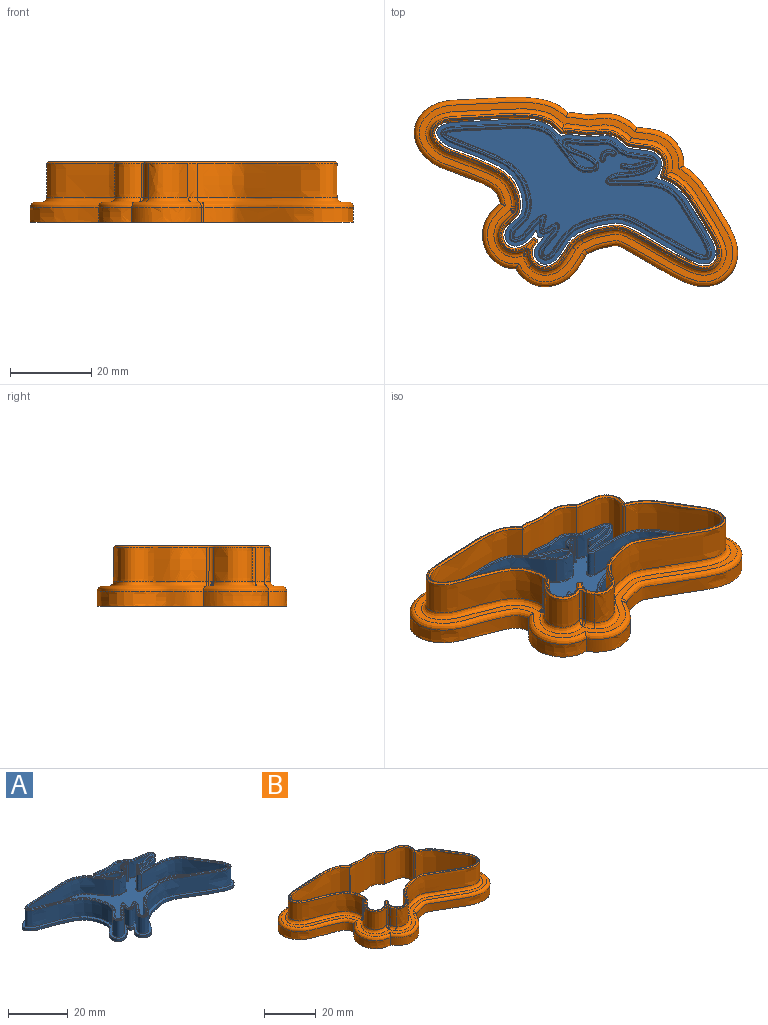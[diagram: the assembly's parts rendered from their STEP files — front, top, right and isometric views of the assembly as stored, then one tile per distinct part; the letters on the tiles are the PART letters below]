
ASSEMBLY  parts=2 mates=1
PART A: 95 faces, bbox 69x37.9x8.3 mm
  f0: plane 64.33x31.4mm, normal (0,0,1), area 715.8mm2, adj f40,f41,f42,f43,f45,f46,f47,f48
  f1: plane 68.72x35.77mm, normal (0,0,1), area 203.8mm2, adj f2,f3,f4,f5,f7,f8,f9,f10
  f2: extruded ~33.7x21.08mm, area 61mm2, adj f1,f3,f5,f6
  f3: extruded ~8.98x7.79mm, area 14.8mm2, adj f1,f2,f4,f6
  f4: extruded ~15.66x2.98mm, area 16.7mm2, adj f1,f3,f5,f6
  f5: extruded ~35.59x34.48mm, area 107.2mm2, adj f1,f2,f4,f6
  f6: plane 68.72x35.77mm, normal (0,0,-1), area 1212.7mm2, adj f2,f3,f4,f5
  f7: extruded ~14.82x6.75mm, area 110.2mm2, adj f1,f8,f26,f93
  f8: extruded ~6.75x0.94mm, area 8.2mm2, adj f1,f7,f9,f94
  f9: extruded ~29.13x29mm, area 500.5mm2, adj f1,f8,f10,f92
  f10: extruded ~12.57x9.63mm, area 227mm2, adj f1,f9,f11,f90
  f11: extruded ~33.3x19.43mm, area 477.3mm2, adj f1,f10,f12,f88
  f12: extruded ~6.75x5.65mm, area 40.1mm2, adj f1,f11,f26,f89
  f13: extruded ~6.75x6.69mm, area 61.7mm2, adj f24,f28,f86
  f14: extruded ~6.91x6.55mm, area 46.4mm2, adj f25,f38,f49,f78
  f15: plane 6.55x0.2mm, normal (-0.98,0.2,0), area 1.3mm2, adj f38,f39,f53,f82
  f16: extruded ~7.34x6.55mm, area 49.3mm2, adj f17,f39,f52,f85
  f17: extruded ~11.25x6.55mm, area 92mm2, adj f16,f18,f50,f83
  f18: extruded ~32.77x17.49mm, area 454.1mm2, adj f17,f19,f48,f81
  f19: extruded ~8.01x7.84mm, area 158.9mm2, adj f18,f20,f46,f55,f79
  f20: extruded ~7.96x6.55mm, area 133.7mm2, adj f19,f21,f43,f56,f77
  f21: extruded ~32.03x22.02mm, area 455.2mm2, adj f20,f22,f41,f75
  f22: extruded ~6.55x5.59mm, area 50.1mm2, adj f21,f23,f40,f73
  f23: extruded ~13.1x6.55mm, area 150.1mm2, adj f22,f25,f42,f44,f45,f74
  f24: extruded ~6.75x6.54mm, area 49.9mm2, adj f13,f28,f87
  f25: extruded ~7.89x6.55mm, area 53.8mm2, adj f14,f23,f47,f76
  f26: extruded ~8.66x6.75mm, area 114.4mm2, adj f1,f7,f12,f91
  f27: plane 66.52x33.57mm, normal (0,0,1), area 116.2mm2, adj f73,f74,f75,f76,f77,f78,f79,f80
  f28: plane 6.73x4.29mm, normal (0,0,1), area 10.6mm2, adj f13,f24
  f29: cylinder r=2.1mm len=6.55mm, axis (0,0,-1), area 34.6mm2, adj f34,f37,f62,f70
  f30: plane 6.55x0.19mm, normal (0.38,-0.92,0), area 1.4mm2, adj f34,f35,f58,f71
  f31: cylinder r=1.1mm len=6.55mm, axis (0,0,-1), area 17.6mm2, adj f35,f36,f59,f67
  f32: plane 6.55x0.18mm, normal (0.52,-0.85,0), area 1.4mm2, adj f36,f37,f63,f66
  f33: plane 3.21x2.26mm, normal (0,0,1), area 2.1mm2, adj f65,f66,f67,f68,f69,f70,f71,f72
  f34: cylinder r=0.4mm len=6.55mm, axis (0,0,-1), area 4.7mm2, adj f29,f30,f60,f72
  f35: cylinder r=0.4mm len=6.55mm, axis (0,0,-1), area 3.4mm2, adj f30,f31,f57,f69
  f36: cylinder r=0.4mm len=6.55mm, axis (0,0,-1), area 3.4mm2, adj f31,f32,f61,f65
  f37: cylinder r=0.4mm len=6.55mm, axis (0,0,-1), area 4.7mm2, adj f29,f32,f64,f68
  f38: cylinder r=0.4mm len=6.55mm, axis (0,0,-1), area 4.2mm2, adj f14,f15,f51,f80
  f39: cylinder r=0.4mm len=6.55mm, axis (0,0,-1), area 4.1mm2, adj f15,f16,f54,f84
  f40: bspline ~7.46x2.97mm, area 2.5mm2, adj f0,f22,f41,f42
  f41: bspline ~35.61x32.62mm, area 21.6mm2, adj f0,f21,f40,f43
  f42: bspline ~8.12x4.83mm, area 2.8mm2, adj f0,f23,f40,f44
  f43: bspline ~8.19x5.92mm, area 6.3mm2, adj f0,f20,f41,f56
  f44: bspline ~0.23x0.2mm, area 0mm2, adj f23,f42,f45
  f45: bspline ~13.43x2.87mm, area 4.3mm2, adj f0,f23,f44,f47
  f46: bspline ~8.22x8.06mm, area 7.5mm2, adj f0,f19,f48,f55
  f47: bspline ~9.69x2.92mm, area 2.5mm2, adj f0,f25,f45,f49
  f48: bspline ~34.4x17.55mm, area 21.5mm2, adj f0,f18,f46,f50
  f49: bspline ~8.18x1.43mm, area 2.1mm2, adj f0,f14,f47,f51
  f50: bspline ~11.53x5.49mm, area 4.3mm2, adj f0,f17,f48,f52
  f51: torus R=0.6mm, axis (0,0,1), area 0.2mm2, adj f0,f38,f49,f53
  f52: bspline ~8.18x1.43mm, area 2.2mm2, adj f0,f16,f50,f54
  f53: cylinder r=0.2mm len=0.24mm, axis (0.2,0.98,0), area 0.1mm2, adj f0,f15,f51,f54
  f54: torus R=0.6mm, axis (0,0,1), area 0.2mm2, adj f0,f39,f52,f53
  f55: bspline ~0.23x0.22mm, area 0.1mm2, adj f0,f19,f46,f56
  f56: bspline ~0.27x0.21mm, area 0.1mm2, adj f0,f20,f43,f55
  f57: torus R=0.6mm, axis (0,0,1), area 0.2mm2, adj f0,f35,f58,f59
  f58: cylinder r=0.2mm len=0.27mm, axis (-0.92,-0.38,0), area 0.1mm2, adj f0,f30,f57,f60
  f59: torus R=0.9mm, axis (0,0,1), area 0.8mm2, adj f0,f31,f57,f61
  f60: torus R=0.6mm, axis (0,0,1), area 0.3mm2, adj f0,f34,f58,f62
  f61: torus R=0.6mm, axis (0,0,1), area 0.2mm2, adj f0,f36,f59,f63
  f62: torus R=2.3mm, axis (0,0,1), area 1.7mm2, adj f0,f29,f60,f64
  f63: cylinder r=0.2mm len=0.28mm, axis (-0.85,-0.52,0), area 0.1mm2, adj f0,f32,f61,f64
  f64: torus R=0.6mm, axis (0,0,1), area 0.3mm2, adj f0,f37,f62,f63
  f65: cone r=0.15mm half-angle=45deg, axis (0,0,-1), area 0.1mm2, adj f33,f36,f66,f67
  f66: plane 0.32x0.31mm, normal (0.37,-0.6,0.71), area 0.1mm2, adj f32,f33,f65,f68
  f67: cone r=1.1mm half-angle=45deg, axis (0,0,1), area 1.1mm2, adj f31,f33,f65,f69
  f68: cone r=0.15mm half-angle=45deg, axis (0,0,-1), area 0.2mm2, adj f33,f37,f66,f70
  f69: cone r=0.15mm half-angle=45deg, axis (0,0,-1), area 0.1mm2, adj f33,f35,f67,f71
  f70: cone r=1.85mm half-angle=45deg, axis (0,0,-1), area 1.8mm2, adj f29,f33,f68,f72
  f71: plane 0.31x0.29mm, normal (0.27,-0.65,0.71), area 0.1mm2, adj f30,f33,f69,f72
  f72: cone r=0.15mm half-angle=45deg, axis (0,0,-1), area 0.2mm2, adj f33,f34,f70,f71
  f73: bspline ~5.89x2.83mm, area 2.6mm2, adj f22,f27,f74,f75
  f74: bspline ~14.37x5.98mm, area 8.2mm2, adj f23,f27,f73,f76
  f75: bspline ~33.93x22.3mm, area 24.5mm2, adj f21,f27,f73,f77
  f76: bspline ~9.64x2.94mm, area 3.1mm2, adj f25,f27,f74,f78
  f77: bspline ~8.25x5.98mm, area 7.3mm2, adj f20,f27,f75,f79
  f78: bspline ~7.89x1.56mm, area 2.7mm2, adj f14,f27,f76,f80
  f79: bspline ~9.14x8.52mm, area 8.6mm2, adj f19,f27,f77,f81
  f80: cone r=0.15mm half-angle=45deg, axis (0,0,-1), area 0.2mm2, adj f27,f38,f78,f82
  f81: bspline ~36.2x18.08mm, area 24.4mm2, adj f18,f27,f79,f83
  f82: plane 0.29x0.25mm, normal (-0.69,0.14,0.71), area 0.1mm2, adj f15,f27,f80,f84
  f83: bspline ~11.94x5.56mm, area 5mm2, adj f17,f27,f81,f85
  f84: cone r=0.15mm half-angle=45deg, axis (0,0,-1), area 0.2mm2, adj f27,f39,f82,f85
  f85: bspline ~8.47x1.63mm, area 2.8mm2, adj f16,f27,f83,f84
  f86: bspline ~8.21x6.06mm, area 3.6mm2, adj f13,f27,f87
  f87: bspline ~7.83x4.3mm, area 2.9mm2, adj f24,f27,f86
  f88: bspline ~36.66x19.6mm, area 25.1mm2, adj f11,f27,f89,f90
  f89: bspline ~5.93x1.55mm, area 2.2mm2, adj f12,f27,f88,f91
  f90: bspline ~15.06x9.95mm, area 12mm2, adj f10,f27,f88,f92
  f91: bspline ~9.51x7.14mm, area 5.9mm2, adj f26,f27,f89,f93
  f92: bspline ~29.31x29.09mm, area 26.2mm2, adj f9,f27,f90,f94
  f93: bspline ~15.44x3.46mm, area 5.8mm2, adj f7,f27,f91,f94
  f94: bspline ~1.66x1.39mm, area 0.6mm2, adj f8,f27,f92,f93
PART B: 79 faces, bbox 80.2x47.2x15.6 mm
  f0: extruded ~9.69x8.4mm, area 107.7mm2, adj f1,f10,f41,f65
  f1: extruded ~8.4x2.09mm, area 20mm2, adj f0,f2,f43,f67
  f2: extruded ~8.4x0.97mm, area 8.2mm2, adj f1,f32,f45,f69
  f3: extruded ~9.54x8.4mm, area 132mm2, adj f4,f32,f42,f70
  f4: extruded ~8.4x1.15mm, area 11.4mm2, adj f3,f5,f40,f64,f66,f68
  f5: plane 8.4x0.51mm, normal (-0.99,0.15,0), area 4.3mm2, adj f4,f6,f38,f62
  f6: extruded ~32.44x23.02mm, area 547mm2, adj f5,f7,f36,f60,f62
  f7: extruded ~16.31x8.4mm, area 145.8mm2, adj f6,f8,f34,f58
  f8: extruded ~9.58x8.4mm, area 125.6mm2, adj f7,f9,f35,f59
  f9: extruded ~34.57x23.25mm, area 526.2mm2, adj f8,f10,f37,f61
  f10: extruded ~8.4x2.23mm, area 25.5mm2, adj f0,f9,f39,f63
  f11: extruded ~14.6x4.88mm, area 80.2mm2, adj f12,f20,f33,f57
  f12: extruded ~14.6x10.51mm, area 207.8mm2, adj f11,f13,f20,f55
  f13: extruded ~34.07x21.59mm, area 887.9mm2, adj f12,f20,f29,f53
  f14: extruded ~14.6x9.18mm, area 206mm2, adj f15,f20,f29,f49
  f15: extruded ~15.64x14.6mm, area 243.3mm2, adj f14,f20,f30,f47
  f16: extruded ~31.01x22.69mm, area 942.3mm2, adj f17,f20,f30,f48
  f17: extruded ~14.6x9.53mm, area 260.8mm2, adj f16,f20,f31,f50
  f18: extruded ~14.6x0.17mm, area 3.2mm2, adj f20,f31,f33,f54
  f19: plane 71.57x38.54mm, normal (0,0,1), area -28.1mm2, adj f34,f35,f36,f37,f38,f39,f40,f41
  f20: plane 79.62x46.69mm, normal (0,0,-1), area 1004.3mm2, adj f11,f12,f13,f14,f15,f16,f17,f18
  f21: extruded ~37.73x26.17mm, area 263.2mm2, adj f20,f22,f27,f77
  f22: extruded ~16.99x3.8mm, area 68.3mm2, adj f20,f21,f23,f75
  f23: extruded ~11.52x9.5mm, area 64mm2, adj f20,f22,f24,f73
  f24: extruded ~36.84x29.46mm, area 307.4mm2, adj f20,f23,f25,f72
  f25: plane 3.8x0.67mm, normal (0.73,-0.69,0), area 3.5mm2, adj f20,f24,f26,f74
  f26: extruded ~17.1x7.52mm, area 83.6mm2, adj f20,f25,f27,f76
  f27: extruded ~16.05x8.23mm, area 84.5mm2, adj f20,f21,f26,f78
  f28: plane 77.22x44.29mm, normal (0,0,1), area 336.7mm2, adj f58,f59,f60,f61,f62,f63,f64,f65
  f29: cylinder r=0.5mm len=14.6mm, axis (0,0,-1), area 12.9mm2, adj f13,f14,f20,f51
  f30: cylinder r=0.5mm len=14.6mm, axis (0,0,-1), area 8.2mm2, adj f15,f16,f20,f46
  f31: cylinder r=0.5mm len=14.6mm, axis (0,0,-1), area 12.8mm2, adj f17,f18,f20,f52
  f32: cylinder r=0.5mm len=8.4mm, axis (0,0,-1), area 8.9mm2, adj f2,f3,f44,f71
  f33: cylinder r=0.5mm len=14.6mm, axis (0,0,-1), area 12.7mm2, adj f11,f18,f20,f56
  f34: bspline ~17.62x4.2mm, area 9.8mm2, adj f7,f19,f35,f36
  f35: bspline ~10.23x9.39mm, area 8.4mm2, adj f8,f19,f34,f37
  f36: bspline ~33.98x24.89mm, area 36.7mm2, adj f6,f19,f34,f38
  f37: bspline ~37.66x24.27mm, area 35.8mm2, adj f9,f19,f35,f39
  f38: plane 0.58x0.47mm, normal (-0.7,0.1,0.71), area 0.3mm2, adj f5,f19,f36,f40
  f39: bspline ~2.72x2.47mm, area 1.8mm2, adj f10,f19,f37,f41
  f40: bspline ~1.48x1.02mm, area 0.8mm2, adj f4,f19,f38,f42
  f41: bspline ~9.69x6.02mm, area 7mm2, adj f0,f19,f39,f43
  f42: bspline ~9.59x6.51mm, area 8.6mm2, adj f3,f19,f40,f44
  f43: bspline ~2.17x1.37mm, area 1.3mm2, adj f1,f19,f41,f45
  f44: cone r=0.9mm half-angle=45deg, axis (0,0,1), area 0.8mm2, adj f19,f32,f42,f45
  f45: bspline ~0.97x0.48mm, area 0.5mm2, adj f2,f19,f43,f44
  f46: cone r=0.1mm half-angle=45deg, axis (0,0,-1), area 0.2mm2, adj f19,f30,f47,f48
  f47: bspline ~16.68x4.12mm, area 9.5mm2, adj f15,f19,f46,f49
  f48: bspline ~31.7x23.09mm, area 36.7mm2, adj f16,f19,f46,f50
  f49: bspline ~9.71x7.93mm, area 8.1mm2, adj f14,f19,f47,f51
  f50: bspline ~10.09x8.13mm, area 10.4mm2, adj f17,f19,f48,f52
  f51: cone r=0.1mm half-angle=45deg, axis (0,0,-1), area 0.3mm2, adj f19,f29,f49,f53
  f52: cone r=0.1mm half-angle=45deg, axis (0,0,-1), area 0.3mm2, adj f19,f31,f50,f54
  f53: bspline ~37.39x22.57mm, area 35.8mm2, adj f13,f19,f51,f55
  f54: bspline ~0.49x0.47mm, area 0.2mm2, adj f18,f19,f52,f56
  f55: bspline ~11.04x8.06mm, area 8.2mm2, adj f12,f19,f53,f57
  f56: cone r=0.1mm half-angle=45deg, axis (0,0,-1), area 0.3mm2, adj f19,f33,f54,f57
  f57: bspline ~5.41x1.67mm, area 3.3mm2, adj f11,f19,f55,f56
  f58: bspline ~18.07x4.81mm, area 32.7mm2, adj f7,f28,f59,f60
  f59: bspline ~11.35x10.85mm, area 28.1mm2, adj f8,f28,f58,f61
  f60: bspline ~34.75x25.26mm, area 125mm2, adj f6,f28,f58,f62
  f61: bspline ~37x25.87mm, area 122mm2, adj f9,f28,f59,f63
  f62: cylinder r=1.2mm len=1.26mm, axis (0.15,0.99,0), area 0.9mm2, adj f5,f6,f28,f60,f64
  f63: bspline ~4.07x3.78mm, area 5.4mm2, adj f10,f28,f61,f65
  f64: bspline ~1.38x1.25mm, area 1mm2, adj f4,f28,f62,f66
  f65: bspline ~15.51x8.51mm, area 25.6mm2, adj f0,f28,f63,f67
  f66: bspline ~1.2x1.1mm, area 0.3mm2, adj f4,f64,f68
  f67: bspline ~3.63x2.61mm, area 4.9mm2, adj f1,f28,f65,f69
  f68: bspline ~1.2x1.08mm, area 0.4mm2, adj f4,f28,f66,f70
  f69: bspline ~2.09x1.4mm, area 1.3mm2, adj f2,f28,f67,f71
  f70: bspline ~12.08x8.39mm, area 31.1mm2, adj f3,f28,f68,f71
  f71: bspline ~1.89x1.56mm, area 1mm2, adj f32,f69,f70
  f72: bspline ~39.04x30.36mm, area 131.6mm2, adj f24,f28,f73,f74
  f73: bspline ~12.61x11.49mm, area 31.6mm2, adj f23,f28,f72,f75
  f74: cylinder r=1.2mm len=1.71mm, axis (0.69,0.73,0), area 2mm2, adj f25,f28,f72,f76
  f75: bspline ~18.23x4.99mm, area 34.1mm2, adj f22,f28,f73,f77
  f76: bspline ~18.22x8.64mm, area 40.6mm2, adj f26,f28,f74,f78
  f77: bspline ~38.52x33.51mm, area 135.3mm2, adj f21,f28,f75,f78
  f78: bspline ~16.55x9.23mm, area 41.2mm2, adj f27,f28,f76,f77
PLACE A t=(-24.68,-20.91,4.32)mm
PLACE B t=(-24.71,-20.96,4.32)mm
MATE fastened A.f6 <-> B.f20  axis (0,0,-1) through (-22.88,-6.06,4.32)mm
